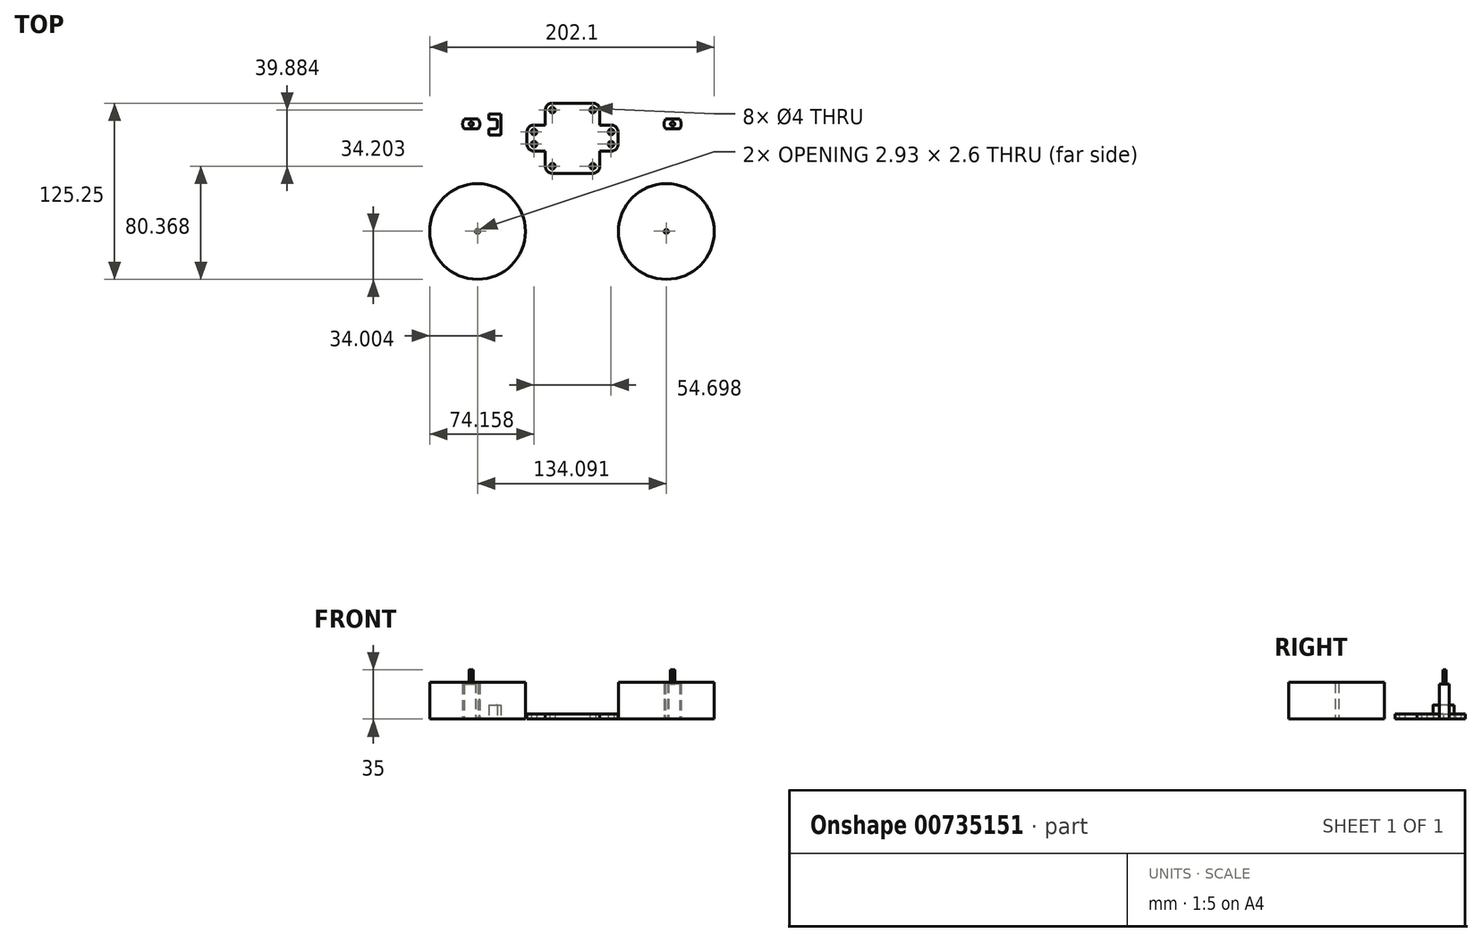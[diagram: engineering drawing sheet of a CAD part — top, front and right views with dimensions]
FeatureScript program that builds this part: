
annotation { "Feature Type Name" : "Feature", "Feature Type Description" : "" }
export const myFeature = defineFeature(function(context is Context, id is Id, definition is map)
    precondition{}
    {
        {
            var Q0;
            Q0=qCreatedBy(makeId("Top.planeOp"),FACE);
            var sketch = newSketch(context, id + "F0", { "sketchPlane" : qUnion([Q0])});
            skCircle(sketch, "E0", {"center": v(-67.05, -31.97) * mm, "radius": 34 * mm});
            skArc(sketch, "E1", {"start": v(-66.02, -33.06) * mm, "mid": v(-67.05, -30.47) * mm, "end": v(-68.07, -33.06) * mm});
            skLineSegment(sketch, "E2", {"start": v(-68.07, -33.06) * mm, "end": v(-66.02, -33.06) * mm});
            skSolve(sketch);
        }
        {
            var Q0;
            Q0=makeQuery(id+"F0.imprint","IMPRINT",FACE,{"disambiguationData":[TD([[makeQuery(id+"F0.imprint","IMPRINT",EDGE,{"derivedFrom":sQuery(id+"F0.wireOp",EDGE,"E0")}),1.0]])]});
            extrude(context, id + "F1", {"entities" : qUnion([Q0]), "depth" : 26 * mm, "offsetDistance" : 25 * mm});
        }
        {
            var Q0;
            Q0 = qSketchRegion(id + "F0", true);
            extrude(context, id + "F2", {"entities" : qUnion([Q0]), "operationType" : NewBodyOperationType.ADD, "depth" : 25 * mm, "offsetDistance" : 25 * mm});
        }
        {
            var Q0;
            Q0=qCreatedBy(makeId("Top.planeOp"),FACE);
            var sketch = newSketch(context, id + "F3", { "sketchPlane" : qUnion([Q0])});
            skArc(sketch, "E3", {"start": v(-76.51, 47.88) * mm, "mid": v(-77.62, 44.38) * mm, "end": v(-76.51, 40.88) * mm});
            skLineSegment(sketch, "E4", {"start": v(-76.51, 40.88) * mm, "end": v(-66.51, 40.88) * mm});
            skLineSegment(sketch, "E5", {"start": v(-76.51, 47.88) * mm, "end": v(-66.51, 47.88) * mm});
            skArc(sketch, "E6.trimOffspring", {"start": v(-66.51, 40.88) * mm, "mid": v(-65.41, 44.38) * mm, "end": v(-66.51, 47.88) * mm});
            skSolve(sketch);
        }
        {
            var Q0;
            Q0 = qSketchRegion(id + "F3", true);
            extrude(context, id + "F4", {"entities" : qUnion([Q0]), "depth" : 25 * mm, "offsetDistance" : 25 * mm});
        }
        {
            var Q0;
            Q0=makeQuery(id+"F4.opExtrude","CAP_FACE",FACE,{"disambiguationData":[OSD([sQuery(id+"F3.wireOp",EDGE,"E3"),sQuery(id+"F3.wireOp",EDGE,"E4"),sQuery(id+"F3.wireOp",EDGE,"E5"),sQuery(id+"F3.wireOp",EDGE,"E6.trimOffspring")])],"isStart":false});
            var sketch = newSketch(context, id + "F5", { "sketchPlane" : qUnion([Q0])});
            skArc(sketch, "E7", {"start": v(-70.4, 43.37) * mm, "mid": v(-71.51, 45.88) * mm, "end": v(-72.62, 43.37) * mm});
            skLineSegment(sketch, "E8", {"start": v(-71.51, 43.38) * mm, "end": v(-72.62, 43.37) * mm});
            skLineSegment(sketch, "E9", {"start": v(-72.62, 43.37) * mm, "end": v(-70.4, 43.37) * mm});
            skSolve(sketch);
        }
        {
            var Q0;
            Q0 = qSketchRegion(id + "F5", true);
            extrude(context, id + "F6", {"entities" : qUnion([Q0]), "operationType" : NewBodyOperationType.ADD, "depth" : 10 * mm, "offsetDistance" : 25 * mm});
        }
        {
            var Q0;
            Q0=makeQuery(id+"F4.opExtrude","SWEPT_BODY",BODY,{"disambiguationData":[OSD([sQuery(id+"F3.wireOp",EDGE,"E3"),sQuery(id+"F3.wireOp",EDGE,"E4"),sQuery(id+"F3.wireOp",EDGE,"E5"),sQuery(id+"F3.wireOp",EDGE,"E6.trimOffspring")])]});
            var Q1;
            Q1=makeQuery(id+"F1.opExtrude","SWEPT_BODY",BODY,{"disambiguationData":[OSD([sQuery(id+"F0.wireOp",EDGE,"E0"),sQuery(id+"F0.wireOp",EDGE,"E1"),sQuery(id+"F0.wireOp",EDGE,"E2")])]});
            var Q2;
            Q2=qCreatedBy(makeId("Right.planeOp"),FACE);
            mirror(context, id + "F7", {"entities" : qUnion([Q0, Q1]), "mirrorPlane" : qUnion([Q2])});
        }
        {
            var Q0;
            Q0=qCreatedBy(makeId("Top.planeOp"),FACE);
            var sketch = newSketch(context, id + "F8", { "sketchPlane" : qUnion([Q0])});
            skLineSegment(sketch, "E10.bottom", {"start": v(-59.11, 41.14) * mm, "end": v(-59.11, 41.14) * mm});
            skLineSegment(sketch, "E10.top", {"start": v(-59.11, 36.53) * mm, "end": v(-59.11, 36.53) * mm});
            skLineSegment(sketch, "E10.left", {"start": v(-59.11, 41.14) * mm, "end": v(-59.11, 36.53) * mm});
            skLineSegment(sketch, "E10.right", {"start": v(-59.11, 41.14) * mm, "end": v(-59.11, 36.53) * mm});
            skLineSegment(sketch, "E11.bottom", {"start": v(-59.11, 47.55) * mm, "end": v(-59.11, 47.55) * mm});
            skLineSegment(sketch, "E11.top", {"start": v(-59.11, 51.56) * mm, "end": v(-59.11, 51.56) * mm});
            skLineSegment(sketch, "E11.left", {"start": v(-59.11, 47.55) * mm, "end": v(-59.11, 51.56) * mm});
            skLineSegment(sketch, "E11.right", {"start": v(-59.11, 47.55) * mm, "end": v(-59.11, 51.56) * mm});
            skLineSegment(sketch, "E12.bottom", {"start": v(-59.11, 51.56) * mm, "end": v(-50.3, 51.56) * mm});
            skLineSegment(sketch, "E12.top", {"start": v(-59.11, 51.56) * mm, "end": v(-50.3, 51.56) * mm});
            skLineSegment(sketch, "E12.right", {"start": v(-50.3, 51.56) * mm, "end": v(-50.3, 51.56) * mm});
            skLineSegment(sketch, "E13.top", {"start": v(-50.3, 36.13) * mm, "end": v(-50.3, 36.13) * mm});
            skLineSegment(sketch, "E13.left", {"start": v(-50.3, 51.56) * mm, "end": v(-50.3, 36.53) * mm});
            skLineSegment(sketch, "E13.right", {"start": v(-50.3, 51.56) * mm, "end": v(-50.3, 36.53) * mm});
            skLineSegment(sketch, "E14", {"start": v(-59.11, 47.55) * mm, "end": v(-52.86, 47.55) * mm});
            skLineSegment(sketch, "E15", {"start": v(-52.86, 47.55) * mm, "end": v(-52.86, 41.14) * mm});
            skLineSegment(sketch, "E16", {"start": v(-52.86, 41.14) * mm, "end": v(-59.11, 41.14) * mm});
            skLineSegment(sketch, "E17", {"start": v(-59.11, 36.53) * mm, "end": v(-50.3, 36.53) * mm});
            skLineSegment(sketch, "E18", {"start": v(-50.3, 36.53) * mm, "end": v(-50.3, 51.56) * mm});
            skSolve(sketch);
        }
        {
            var Q0;
            Q0 = qSketchRegion(id + "F8", true);
            extrude(context, id + "F9", {"entities" : qUnion([Q0]), "depth" : 10 * mm, "offsetDistance" : 25 * mm});
        }
        {
            var Q0;
            Q0=makeQuery(id+"F9.opExtrude","SWEPT_EDGE",EDGE,{"disambiguationData":[OSD([sQuery(id+"F8.wireOp",EDGE,"E11.right"),sQuery(id+"F8.wireOp",EDGE,"E14")])]});
            var Q1;
            Q1=makeQuery(id+"F9.opExtrude","SWEPT_EDGE",EDGE,{"disambiguationData":[OSD([sQuery(id+"F8.wireOp",EDGE,"E10.right"),sQuery(id+"F8.wireOp",EDGE,"E16")])]});
            var Q2;
            Q2=makeQuery(id+"F9.opExtrude","SWEPT_EDGE",EDGE,{"disambiguationData":[OSD([sQuery(id+"F8.wireOp",EDGE,"E14"),sQuery(id+"F8.wireOp",EDGE,"E15")])]});
            var Q3;
            Q3=makeQuery(id+"F9.opExtrude","SWEPT_EDGE",EDGE,{"disambiguationData":[OSD([sQuery(id+"F8.wireOp",EDGE,"E15"),sQuery(id+"F8.wireOp",EDGE,"E16")])]});
            var Q4;
            Q4=makeQuery(id+"F9.opExtrude","SWEPT_EDGE",EDGE,{"disambiguationData":[OSD([sQuery(id+"F8.wireOp",EDGE,"E12.top"),sQuery(id+"F8.wireOp",EDGE,"E18")])]});
            var Q5;
            Q5=makeQuery(id+"F9.opExtrude","SWEPT_EDGE",EDGE,{"disambiguationData":[OSD([sQuery(id+"F8.wireOp",EDGE,"E11.right"),sQuery(id+"F8.wireOp",EDGE,"E12.top")])]});
            var Q6;
            Q6=makeQuery(id+"F9.opExtrude","SWEPT_EDGE",EDGE,{"disambiguationData":[OSD([sQuery(id+"F8.wireOp",EDGE,"E17"),sQuery(id+"F8.wireOp",EDGE,"E18")])]});
            var Q7;
            Q7=makeQuery(id+"F9.opExtrude","SWEPT_EDGE",EDGE,{"disambiguationData":[OSD([sQuery(id+"F8.wireOp",EDGE,"E10.right"),sQuery(id+"F8.wireOp",EDGE,"E17")])]});
            fillet(context, id + "F10", {"entities" : qUnion([Q0, Q1, Q2, Q3, Q4, Q5, Q6, Q7]), "radius" : 1.2 * mm, "tangentPropagation" : true, "allowEdgeOverflow" : false});
        }
        {
            var Q0;
            Q0=qCreatedBy(makeId("Top.planeOp"),FACE);
            var sketch = newSketch(context, id + "F11", { "sketchPlane" : qUnion([Q0])});
            skLineSegment(sketch, "E19.bottom", {"start": v(-13.9, 9.4) * mm, "end": v(14.8, 9.4) * mm});
            skLineSegment(sketch, "E19.top", {"start": v(-13.9, 59.28) * mm, "end": v(14.8, 59.28) * mm});
            skLineSegment(sketch, "E19.left", {"start": v(-18.9, 14.4) * mm, "end": v(-18.9, 25.12) * mm});
            skLineSegment(sketch, "E19.right", {"start": v(19.8, 14.4) * mm, "end": v(19.8, 25.12) * mm});
            skLineSegment(sketch, "E20.bottom", {"start": v(-18.9, 43.71) * mm, "end": v(-26.9, 43.71) * mm});
            skLineSegment(sketch, "E20.top", {"start": v(-18.9, 25.12) * mm, "end": v(-26.9, 25.12) * mm});
            skLineSegment(sketch, "E20.right", {"start": v(-31.9, 38.71) * mm, "end": v(-31.9, 30.12) * mm});
            skLineSegment(sketch, "E21.bottom", {"start": v(19.8, 43.71) * mm, "end": v(27.8, 43.71) * mm});
            skLineSegment(sketch, "E21.top", {"start": v(19.8, 25.12) * mm, "end": v(27.8, 25.12) * mm});
            skLineSegment(sketch, "E21.right", {"start": v(32.8, 38.71) * mm, "end": v(32.8, 30.12) * mm});
            skPoint(sketch, "E22.visualSharp", {"position": v(-18.9, 59.28) * mm});
            skArc(sketch, "E22.filletArc", {"start": v(-13.9, 59.28) * mm, "mid": v(-17.43, 57.82) * mm, "end": v(-18.9, 54.28) * mm});
            skPoint(sketch, "E23.visualSharp", {"position": v(19.8, 59.28) * mm});
            skArc(sketch, "E23.filletArc", {"start": v(19.8, 54.28) * mm, "mid": v(18.34, 57.82) * mm, "end": v(14.8, 59.28) * mm});
            skPoint(sketch, "E24.visualSharp", {"position": v(32.8, 43.71) * mm});
            skArc(sketch, "E24.filletArc", {"start": v(32.8, 38.71) * mm, "mid": v(31.34, 42.25) * mm, "end": v(27.8, 43.71) * mm});
            skPoint(sketch, "E25.visualSharp", {"position": v(32.8, 25.12) * mm});
            skArc(sketch, "E25.filletArc", {"start": v(27.8, 25.12) * mm, "mid": v(31.34, 26.58) * mm, "end": v(32.8, 30.12) * mm});
            skPoint(sketch, "E26.visualSharp", {"position": v(19.8, 9.4) * mm});
            skArc(sketch, "E26.filletArc", {"start": v(14.8, 9.4) * mm, "mid": v(18.34, 10.86) * mm, "end": v(19.8, 14.4) * mm});
            skPoint(sketch, "E27.visualSharp", {"position": v(-18.9, 9.4) * mm});
            skArc(sketch, "E27.filletArc", {"start": v(-18.9, 14.4) * mm, "mid": v(-17.43, 10.86) * mm, "end": v(-13.9, 9.4) * mm});
            skPoint(sketch, "E28.visualSharp", {"position": v(-31.9, 25.12) * mm});
            skArc(sketch, "E28.filletArc", {"start": v(-31.9, 30.12) * mm, "mid": v(-30.43, 26.58) * mm, "end": v(-26.9, 25.12) * mm});
            skPoint(sketch, "E29.visualSharp", {"position": v(-31.9, 43.71) * mm});
            skArc(sketch, "E29.filletArc", {"start": v(-26.9, 43.71) * mm, "mid": v(-30.43, 42.25) * mm, "end": v(-31.9, 38.71) * mm});
            skLineSegment(sketch, "E30.trimOffspring", {"start": v(-18.9, 43.71) * mm, "end": v(-18.9, 54.28) * mm});
            skLineSegment(sketch, "E31.trimOffspring", {"start": v(19.8, 43.71) * mm, "end": v(19.8, 54.28) * mm});
            skCircle(sketch, "E32", {"center": v(-26.9, 38.71) * mm, "radius": 2 * mm});
            skCircle(sketch, "E33", {"center": v(-26.9, 30.12) * mm, "radius": 2 * mm});
            skCircle(sketch, "E34", {"center": v(27.8, 30.12) * mm, "radius": 2 * mm});
            skCircle(sketch, "E35", {"center": v(27.8, 38.71) * mm, "radius": 2 * mm});
            skCircle(sketch, "E36", {"center": v(14.8, 14.4) * mm, "radius": 2 * mm});
            skCircle(sketch, "E37", {"center": v(-13.9, 14.4) * mm, "radius": 2 * mm});
            skCircle(sketch, "E38", {"center": v(-13.9, 54.28) * mm, "radius": 2 * mm});
            skCircle(sketch, "E39", {"center": v(14.8, 54.28) * mm, "radius": 2 * mm});
            skSolve(sketch);
        }
        {
            var Q0;
            Q0 = qSketchRegion(id + "F11", true);
            extrude(context, id + "F12", {"entities" : qUnion([Q0]), "depth" : 3.5 * mm, "offsetDistance" : 25 * mm});
        }
    });
